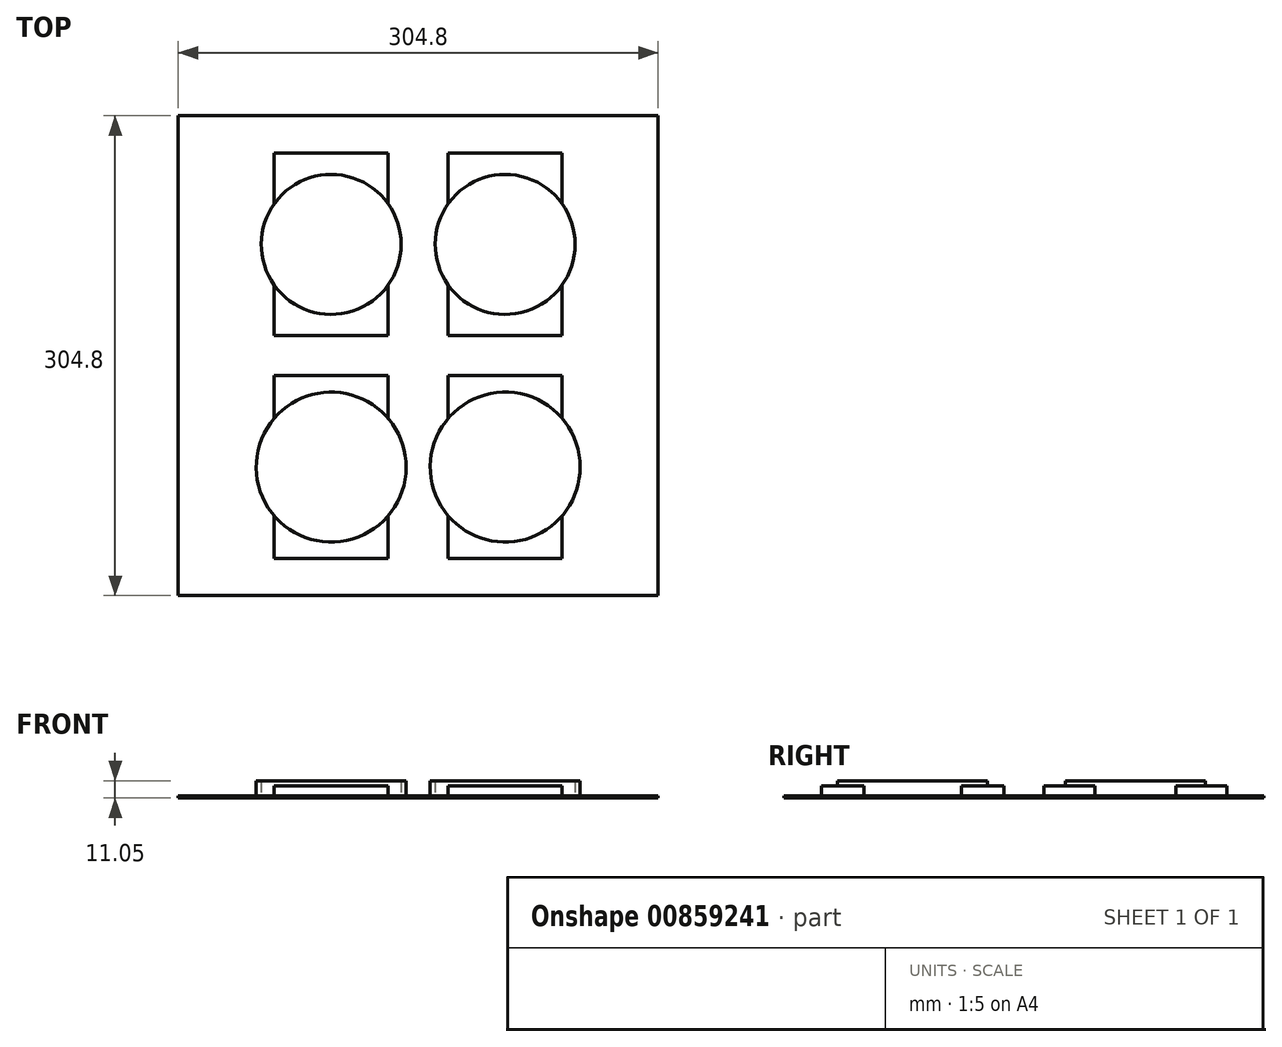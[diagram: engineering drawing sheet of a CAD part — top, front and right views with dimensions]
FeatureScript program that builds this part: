
annotation { "Feature Type Name" : "Feature", "Feature Type Description" : "" }
export const myFeature = defineFeature(function(context is Context, id is Id, definition is map)
    precondition{}
    {
        {
            var Q0;
            Q0=qCreatedBy(makeId("Top.planeOp"),FACE);
            var sketch = newSketch(context, id + "F0", { "sketchPlane" : qUnion([Q0])});
            skLineSegment(sketch, "E0.bottom", {"start": v(-152.4, 152.4) * mm, "end": v(152.4, 152.4) * mm});
            skLineSegment(sketch, "E0.top", {"start": v(-152.4, -152.4) * mm, "end": v(152.4, -152.4) * mm});
            skLineSegment(sketch, "E0.left", {"start": v(-152.4, 152.4) * mm, "end": v(-152.4, -152.4) * mm});
            skLineSegment(sketch, "E0.right", {"start": v(152.4, 152.4) * mm, "end": v(152.4, -152.4) * mm});
            skPoint(sketch, "E1", {"position": v(0, 152.4) * mm});
            skPoint(sketch, "E2", {"position": v(152.4, 0) * mm});
            skSolve(sketch);
        }
        {
            var Q0;
            Q0 = qSketchRegion(id + "F0", true);
            extrude(context, id + "F1", {"entities" : qUnion([Q0]), "depth" : 1.52 * mm, "offsetDistance" : 25.4 * mm});
        }
        {
            var Q0;
            Q0=makeQuery(id+"F1.opExtrude","CAP_FACE",FACE,{"disambiguationData":[OSD([sQuery(id+"F0.wireOp",EDGE,"E0.bottom"),sQuery(id+"F0.wireOp",EDGE,"E0.top"),sQuery(id+"F0.wireOp",EDGE,"E0.left"),sQuery(id+"F0.wireOp",EDGE,"E0.right")])],"isStart":false});
            var sketch = newSketch(context, id + "F2", { "sketchPlane" : qUnion([Q0])});
            skLineSegment(sketch, "E3.bottom", {"start": v(-91.44, 128.78) * mm, "end": v(-19.05, 128.78) * mm});
            skLineSegment(sketch, "E3.top", {"start": v(-91.44, 12.7) * mm, "end": v(-19.05, 12.7) * mm});
            skLineSegment(sketch, "E3.left", {"start": v(-91.44, 128.78) * mm, "end": v(-91.44, 12.7) * mm});
            skLineSegment(sketch, "E3.right", {"start": v(-19.05, 128.78) * mm, "end": v(-19.05, 12.7) * mm});
            skLineSegment(sketch, "E4.bottom", {"start": v(19.05, 128.78) * mm, "end": v(91.44, 128.78) * mm});
            skLineSegment(sketch, "E4.top", {"start": v(19.05, 12.7) * mm, "end": v(91.44, 12.7) * mm});
            skLineSegment(sketch, "E4.left", {"start": v(19.05, 128.78) * mm, "end": v(19.05, 12.7) * mm});
            skLineSegment(sketch, "E4.right", {"start": v(91.44, 128.78) * mm, "end": v(91.44, 12.7) * mm});
            skLineSegment(sketch, "E5.bottom", {"start": v(-91.44, -12.7) * mm, "end": v(-19.05, -12.7) * mm});
            skLineSegment(sketch, "E5.top", {"start": v(-91.44, -128.78) * mm, "end": v(-19.05, -128.78) * mm});
            skLineSegment(sketch, "E5.left", {"start": v(-91.44, -12.7) * mm, "end": v(-91.44, -128.78) * mm});
            skLineSegment(sketch, "E5.right", {"start": v(-19.05, -12.7) * mm, "end": v(-19.05, -128.78) * mm});
            skLineSegment(sketch, "E6.bottom", {"start": v(19.05, -12.7) * mm, "end": v(91.44, -12.7) * mm});
            skLineSegment(sketch, "E6.top", {"start": v(19.05, -128.78) * mm, "end": v(91.44, -128.78) * mm});
            skLineSegment(sketch, "E6.left", {"start": v(19.05, -12.7) * mm, "end": v(19.05, -128.78) * mm});
            skLineSegment(sketch, "E6.right", {"start": v(91.44, -12.7) * mm, "end": v(91.44, -128.78) * mm});
            skLineSegment(sketch, "E7", {"start": v(-91.44, 70.74) * mm, "end": v(91.44, 70.74) * mm, "construction": true});
            skLineSegment(sketch, "E8", {"start": v(-91.44, -70.74) * mm, "end": v(91.44, -70.74) * mm, "construction": true});
            skLineSegment(sketch, "E9", {"start": v(-55.24, 128.78) * mm, "end": v(-55.24, -128.78) * mm, "construction": true});
            skLineSegment(sketch, "E10", {"start": v(55.25, 128.78) * mm, "end": v(55.24, -128.78) * mm, "construction": true});
            skPoint(sketch, "E11", {"position": v(-55.24, 70.74) * mm});
            skPoint(sketch, "E12", {"position": v(55.25, 70.74) * mm});
            skPoint(sketch, "E13", {"position": v(55.24, -70.74) * mm});
            skPoint(sketch, "E14", {"position": v(-55.24, -70.74) * mm});
            skSolve(sketch);
        }
        {
            var Q0;
            Q0 = qSketchRegion(id + "F2", true);
            extrude(context, id + "F3", {"entities" : qUnion([Q0]), "operationType" : NewBodyOperationType.ADD, "depth" : 6.35 * mm, "offsetDistance" : 25.4 * mm});
        }
        {
            var Q0;
            Q0=makeQuery(id+"F1.opExtrude","CAP_FACE",FACE,{"disambiguationData":[OSD([sQuery(id+"F0.wireOp",EDGE,"E0.bottom"),sQuery(id+"F0.wireOp",EDGE,"E0.top"),sQuery(id+"F0.wireOp",EDGE,"E0.left"),sQuery(id+"F0.wireOp",EDGE,"E0.right")])],"isStart":false});
            var sketch = newSketch(context, id + "F4", { "sketchPlane" : qUnion([Q0])});
            skLineSegment(sketch, "E15", {"start": v(-91.44, 70.74) * mm, "end": v(91.44, 70.74) * mm, "construction": true});
            skLineSegment(sketch, "E16", {"start": v(-91.44, -70.74) * mm, "end": v(91.44, -70.74) * mm, "construction": true});
            skLineSegment(sketch, "E17", {"start": v(-55.24, 128.78) * mm, "end": v(-55.24, -128.78) * mm, "construction": true});
            skLineSegment(sketch, "E18", {"start": v(55.25, 128.78) * mm, "end": v(55.24, -128.78) * mm, "construction": true});
            skCircle(sketch, "E19", {"center": v(-55.24, 70.74) * mm, "radius": 44.45 * mm});
            skCircle(sketch, "E20", {"center": v(55.25, 70.74) * mm, "radius": 44.45 * mm});
            skCircle(sketch, "E21", {"center": v(-55.24, -70.74) * mm, "radius": 47.63 * mm});
            skCircle(sketch, "E22", {"center": v(55.24, -70.74) * mm, "radius": 47.63 * mm});
            skSolve(sketch);
        }
        {
            var Q0;
            Q0 = qSketchRegion(id + "F4", true);
            extrude(context, id + "F5", {"entities" : qUnion([Q0]), "operationType" : NewBodyOperationType.ADD, "depth" : 9.52 * mm, "offsetDistance" : 25.4 * mm});
        }
    });
